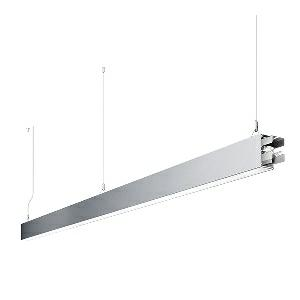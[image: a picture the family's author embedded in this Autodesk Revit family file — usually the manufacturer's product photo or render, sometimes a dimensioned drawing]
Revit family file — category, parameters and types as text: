
# Revit family: dotoo_line_-_dlp_3000_840_d_sta_00805830_2714
name_source: partatom
category: Lighting Fixtures
units: mm (PartAtom-declared; Revit-internal decimal feet)

## family parameters
Cut with Voids When Loaded = No
Host = Face
Light Source = No
Part Type = Normal
Room Calculation Point = No
Round Connector Dimension = Use Diameter
Shared = No

## types (1)
- DOTOO.line - DLP 3000/840/D STA (1 x LED, 2750 lm, 4000K)
    Apparent Load = 26 VA
    Approval mark = CE
    CIE Flux Codes = 67 91 98 100 100
    Color Rendering = 80-89
    Color Temperature = 4000K
    Control Gear = Electronic ballast
    Default Elevation = 1800 mm
    Description = DLP 3000/840/D|Suspended luminaire|light source: LED|connected load: 220-240 V, 50/60 Hz|Power consumption: approx. 26 W|standby: approx. 0,15|luminous flux: 2750 lm|luminous efficacy: 105 lm/W|light distribution: Direct|direct ratio: approx. 100 %|colour temperature: Cold white, ca. 4000 K|color rendering index (CRI): >= 80|chromaticity tolerance:  3 SDCM|System of protection: IP 40|technology: Continuously dimmable|luminaire body|material: Sectional aluminium|colour: Silver|lamp cover: Acrylic (PMMA), Clear|mains lead: 2.00 m With free stranded wires|Fastening: Steel cable 0.3 - 0.7 m|glare control: Prism aperture|luminance(L65): <= 3000 cd/m|unified glare rating(4H 8H): <=  19|special features: DALI Load 1x, TouchDIM - dimming via standard switch, Through-wired, up to 18 m on one mains connection, Flicker-free, Suitable as emergency lighting, Start luminaire with mains connection, Mechanical and electrical connection of the individual modules without tools|
    Frequency = 50 Hz
    Height = 110 mm
    Lamp = 1 x LED
    Lamp Light Flux = 2750 lm
    Lamp count = 1
    Length = 2250 mm
    Luminous efficacy = 106 lm/W
    Manufacturer = Waldmann
    ModVariant = No
    Model = 00805830
    Mounting Place = Ceiling
    Mounting Type = Pendant
    Number of Poles = 1
    OnlyDefault = Yes
    Power Factor = 1
    Product Name = DOTOO.line - DLP 3000/840/D STA
    Product group = Suspended luminaire
    ProductGroupID = 9
    Protection Class = Protection class I
    Protection Degree = IP 40
    RLX_Detail_Level = 1
    RLX_Emergency_Light_Flux = 0 lm
    RLX_Emergency_Type = 0
    RLX_Emergency_Type_DB = No
    RlxData = <blob elided: 25145 chars, md5=21d1a18f>
    Socket = socket
    Standby Power = 0 W
    System Light Flux = 2750 lm
    System Power = 26 W
    Type Comments = Product without accessories
    Type Image = 113316000-00692612.jpg
    URL = http://relux.com
    VarID = ---
    Voltage = 230 V
    Voltage Range = 220-240 V
    Weight = 0.00 kg
    Width = 60 mm  [stored 0.19685 ft]

note: [stored X ft] marks values corroborated as IEEE doubles in the binary element streams (Revit-internal decimal feet)

## geometry (parser evidence)
native form markers: Blend x4, Sweep x12
no freeform markers — native parametric forms only
